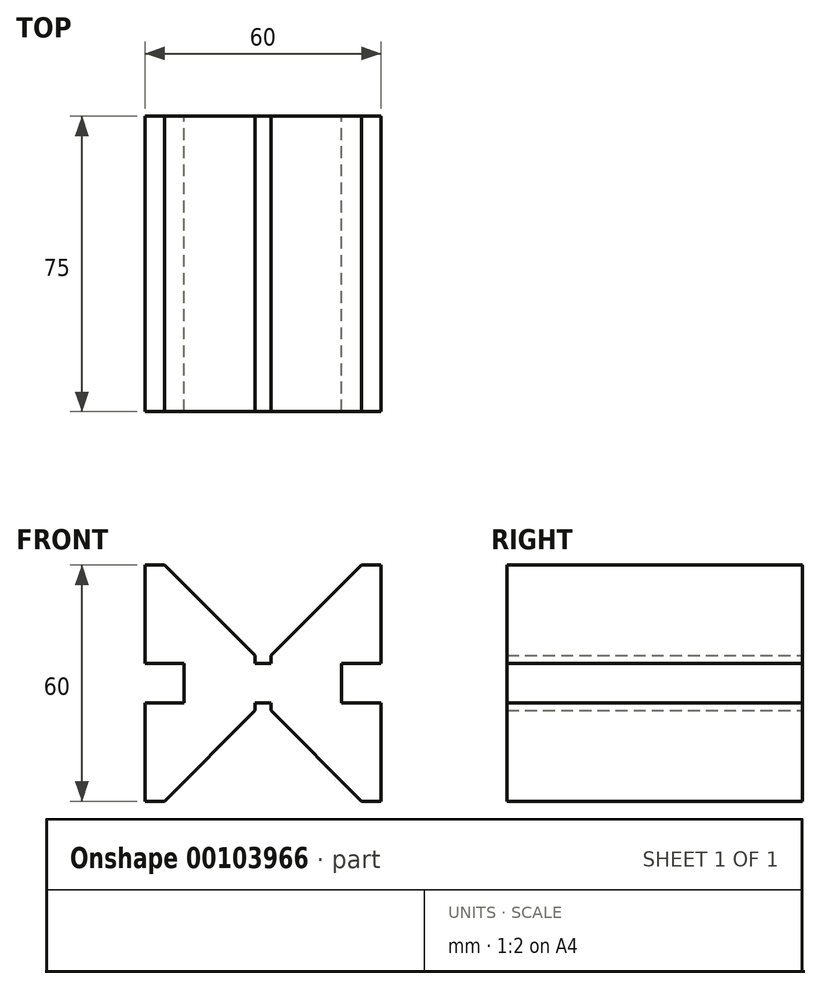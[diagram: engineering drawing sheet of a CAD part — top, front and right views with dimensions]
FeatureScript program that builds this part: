
annotation { "Feature Type Name" : "Feature", "Feature Type Description" : "" }
export const myFeature = defineFeature(function(context is Context, id is Id, definition is map)
    precondition{}
    {
        {
            var Q0;
            Q0=qCreatedBy(makeId("Front.planeOp"),FACE);
            var sketch = newSketch(context, id + "F0", { "sketchPlane" : qUnion([Q0])});
            skLineSegment(sketch, "E0.bottom", {"start": v(0, 0) * mm, "end": v(-30, 0) * mm});
            skLineSegment(sketch, "E0.top", {"start": v(-25, 60) * mm, "end": v(-30, 60) * mm});
            skLineSegment(sketch, "E0.left", {"start": v(0, 25) * mm, "end": v(0, 35) * mm});
            skLineSegment(sketch, "E0.right", {"start": v(-30, 0) * mm, "end": v(-30, 25) * mm});
            skLineSegment(sketch, "E1", {"start": v(-31.43, 25) * mm, "end": v(-20, 25) * mm});
            skLineSegment(sketch, "E2", {"start": v(-31.23, 35) * mm, "end": v(-20, 35) * mm});
            skLineSegment(sketch, "E3", {"start": v(0, 30) * mm, "end": v(-24.33, 30) * mm, "construction": true});
            skPoint(sketch, "E3.endSnap0", {"position": v(0, 30) * mm});
            skLineSegment(sketch, "E4", {"start": v(-2, 35) * mm, "end": v(0, 35) * mm});
            skLineSegment(sketch, "E5", {"start": v(-2, 25) * mm, "end": v(0, 25) * mm});
            skLineSegment(sketch, "E6", {"start": v(-2, 37) * mm, "end": v(-2, 35) * mm});
            skLineSegment(sketch, "E7", {"start": v(-25, 0) * mm, "end": v(-2, 23) * mm});
            skLineSegment(sketch, "E8", {"start": v(-25, 60) * mm, "end": v(-2, 37) * mm});
            skLineSegment(sketch, "E9", {"start": v(-20, 35) * mm, "end": v(-20, 25) * mm});
            skPoint(sketch, "E10.orphan", {"position": v(0, 60) * mm});
            skLineSegment(sketch, "E11.trimOffspring", {"start": v(-30, 35) * mm, "end": v(-30, 60) * mm});
            skLineSegment(sketch, "E12.trimOffspring", {"start": v(-2, 25) * mm, "end": v(-2, 23) * mm});
            skSolve(sketch);
        }
        {
            var Q0;
            Q0=makeQuery(id+"F0.imprint","IMPRINT",FACE,{"disambiguationData":[TD([[makeQuery(id+"F0.imprint","IMPRINT",EDGE,{"derivedFrom":sQuery(id+"F0.wireOp",EDGE,"E0.top")}),1.0]])]});
            extrude(context, id + "F1", {"entities" : qUnion([Q0]), "depth" : 75 * mm});
        }
        {
            var Q0;
            Q0=makeQuery(id+"F1.opExtrude","SWEPT_BODY",BODY,{"disambiguationData":[OSD([sQuery(id+"F0.wireOp",EDGE,"E0.bottom"),sQuery(id+"F0.wireOp",EDGE,"E0.top"),sQuery(id+"F0.wireOp",EDGE,"E0.left"),sQuery(id+"F0.wireOp",EDGE,"E0.right"),sQuery(id+"F0.wireOp",EDGE,"E1"),sQuery(id+"F0.wireOp",EDGE,"E2"),sQuery(id+"F0.wireOp",EDGE,"E4"),sQuery(id+"F0.wireOp",EDGE,"E5"),sQuery(id+"F0.wireOp",EDGE,"E6"),sQuery(id+"F0.wireOp",EDGE,"E7"),sQuery(id+"F0.wireOp",EDGE,"E8"),sQuery(id+"F0.wireOp",EDGE,"E9"),sQuery(id+"F0.wireOp",EDGE,"E11.trimOffspring"),sQuery(id+"F0.wireOp",EDGE,"E12.trimOffspring")])]});
            var Q1;
            Q1=makeQuery(id+"F1.opExtrude","SWEPT_FACE",FACE,{"disambiguationData":[OSD([sQuery(id+"F0.wireOp",EDGE,"E0.left")])]});
            mirror(context, id + "F2", {"operationType" : NewBodyOperationType.ADD, "entities" : qUnion([Q0]), "mirrorPlane" : qUnion([Q1])});
        }
    });
